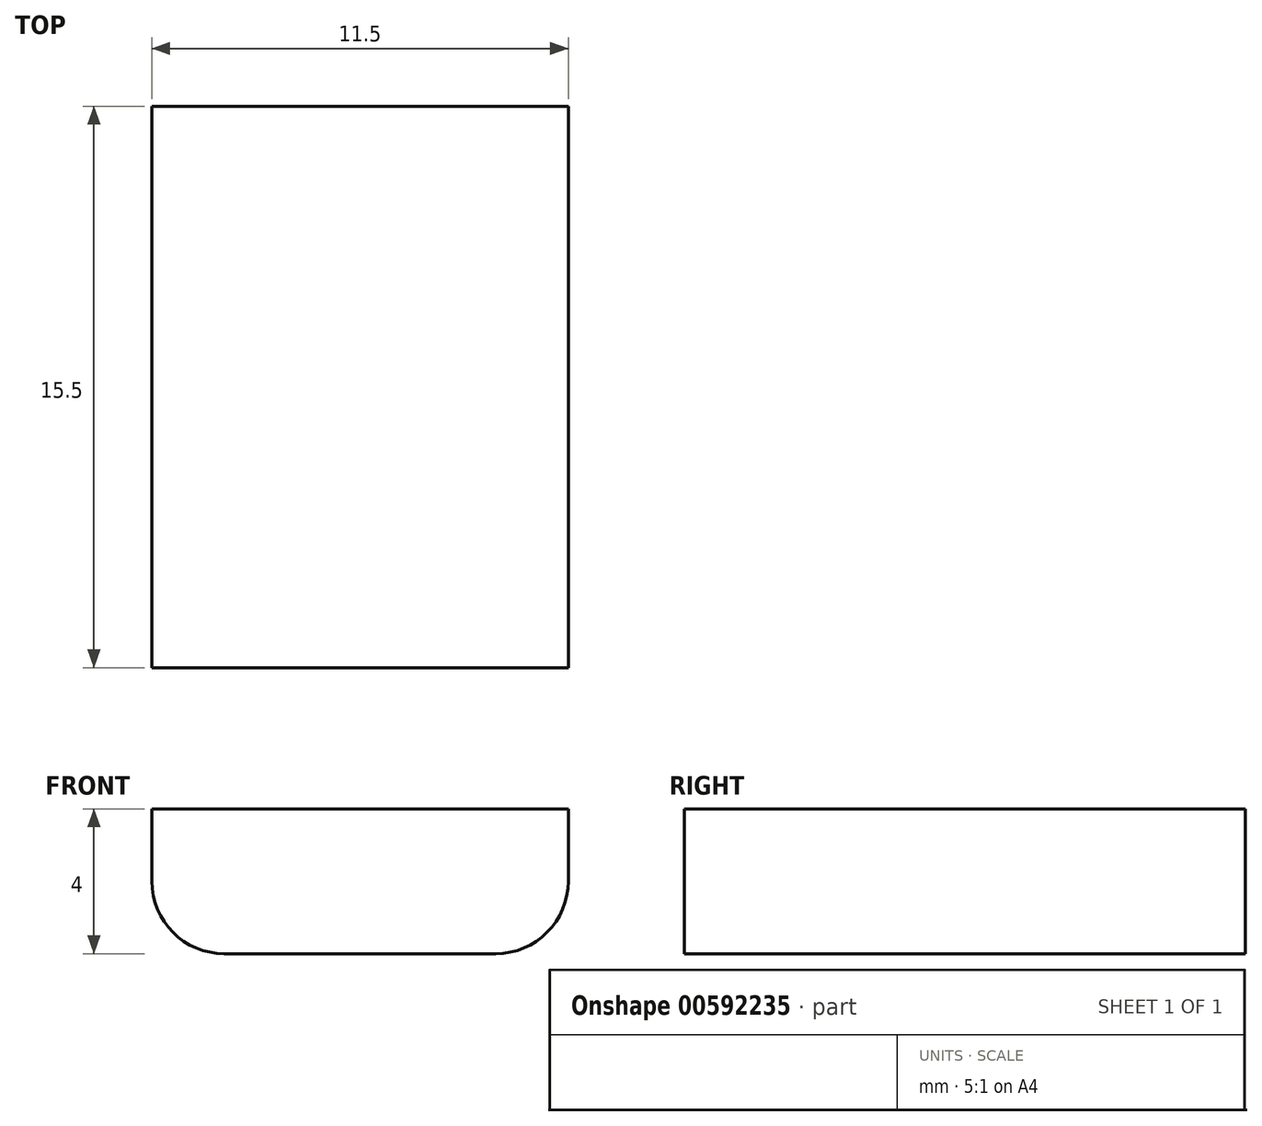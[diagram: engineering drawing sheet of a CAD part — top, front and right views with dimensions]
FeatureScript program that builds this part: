
annotation { "Feature Type Name" : "Feature", "Feature Type Description" : "" }
export const myFeature = defineFeature(function(context is Context, id is Id, definition is map)
    precondition{}
    {
        {
            var Q0;
            Q0=qCreatedBy(makeId("Top.planeOp"),FACE);
            var sketch = newSketch(context, id + "F0", { "sketchPlane" : qUnion([Q0])});
            skLineSegment(sketch, "E0.bottom", {"start": v(5.75, 7.75) * mm, "end": v(-5.75, 7.75) * mm});
            skLineSegment(sketch, "E0.top", {"start": v(5.75, -7.75) * mm, "end": v(-5.75, -7.75) * mm});
            skLineSegment(sketch, "E0.left", {"start": v(5.75, 7.75) * mm, "end": v(5.75, -7.75) * mm});
            skLineSegment(sketch, "E0.right", {"start": v(-5.75, 7.75) * mm, "end": v(-5.75, -7.75) * mm});
            skPoint(sketch, "E0.middle", {"position": v(0, 0) * mm});
            skSolve(sketch);
        }
        {
            var Q0;
            Q0=makeQuery(id+"F0.imprint","IMPRINT",FACE,{"disambiguationData":[TD([[makeQuery(id+"F0.imprint","IMPRINT",EDGE,{"derivedFrom":sQuery(id+"F0.wireOp",EDGE,"E0.bottom")}),1.0]])]});
            extrude(context, id + "F1", {"entities" : qUnion([Q0]), "depth" : 4 * mm, "offsetDistance" : 25 * mm});
        }
        {
            var Q0;
            Q0=makeQuery(id+"F1.opExtrude","CAP_EDGE",EDGE,{"disambiguationData":[OSD([sQuery(id+"F0.wireOp",EDGE,"E0.left")])],"isStart":true});
            var Q1;
            Q1=makeQuery(id+"F1.opExtrude","CAP_EDGE",EDGE,{"disambiguationData":[OSD([sQuery(id+"F0.wireOp",EDGE,"E0.right")])],"isStart":true});
            fillet(context, id + "F2", {"entities" : qUnion([Q0, Q1]), "radius" : 2 * mm, "tangentPropagation" : true, "allowEdgeOverflow" : false});
        }
    });
